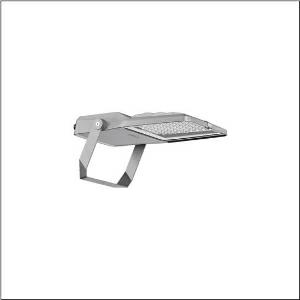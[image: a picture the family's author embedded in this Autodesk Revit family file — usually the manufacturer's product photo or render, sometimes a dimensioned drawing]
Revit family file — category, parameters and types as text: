
# Revit family: floodlight_fl_21_mini___pl64_5xa7776b4e1a_9990
name_source: partatom
category: Lighting Fixtures
units: mm (PartAtom-declared; Revit-internal decimal feet)

## family parameters
Cut with Voids When Loaded = No
Host = Face
Light Source = No
Part Type = Normal
Room Calculation Point = No
Round Connector Dimension = Use Diameter
Shared = No

## types (1)
- --- (1 x LED, 6260 lm, 45.7 W, 4000K)
    Apparent Load = 46 VA
    CIE Flux Codes = 28 80 98 100 100
    Color Rendering = 70
    Color Temperature = 4000K
    Default Elevation = 1800 mm
    Description = Floodlight FL 21 mini, floodlight, primary light control with lens, of PMMA, primary optical cover: protective disc, of toughened safety glass, transparent, light distribution: PL64, light emission: direct distribution, installation type: surface-mounted, LED, High Power LED, rated luminous flux: 6.260lm, luminous efficacy: 137lm/W, light colour: 740, colour temperature: 4000K, control gear: D4iSmart Interface (Zhaga), control: overheat protection, constant luminous flux control, time-dependent luminous flux control, flexible luminous flux parameterisation, pre-setting: logarithmic dimming characteristic, with terminal, 6-pole, mains connection: 220..240V, AC, 50/60Hz, start of lifetime: 46W, end of service life: 48W, reduction: 22W, mounting bracket, of diecast aluminium, powder-coated, Siteco® metallic grey (DB 702S), corrosivity category C5 mid according to DIN EN ISO 12944, suitable for swimming pools, chlorine-resistant, sealing non-destructively replaceable, mounting bracket, of steel, galvanised, powder-coated, Siteco® metallic grey (DB 702S), Smart Interface below and above, protection rating (complete): IP66, insulation class (complete): insulation class II (safety insulation), certification: CE, ENEC, VDE, protection symbol: D, impact resistance: IK08, permissible operating ambient temperature: -40..+40°C, permissible operating ambient temperature for outdoor applications: -40..+50°C, standard: DIN EN 12944, LABS conformity tested according to VDMA 24364:2018-05, packaging unit: 1 piece

Light Distribution: PL64
    Height = 70 mm
    Lamp = 1 x LED
    Lamp Light Flux = 6260 lm
    Lamp Power = 45.7 W
    Lamp count = 1
    Length = 485 mm
    Luminous efficacy = 137 lm/W
    Manufacturer = Siteco
    ModVariant = No
    Model = 5XA7776B4E1A
    Number of Poles = 1
    OnlyDefault = Yes
    Power Factor = 1
    Product Name = Floodlight FL 21 mini | PL64
    Product group = floodlight | pylon annexe
    ProductGroupID = 6200
    Protection Class = Protection class II
    Protection Degree = IP 66
    RLX_Detail_Level = 1
    RLX_Emergency_Light_Flux = 0 lm
    RLX_Emergency_Type = 0
    RLX_Emergency_Type_DB = No
    RlxData = <blob elided: 96001 chars, md5=5dcb8d71>
    Socket = socket
    Standby Power = 0 W
    System Light Flux = 6260 lm
    System Power = 46 W
    Type Comments = factory setting: luminous flux: 100 % | dim-lin: 254 | 463 mA
    Type Image = l_1006845.jpg
    URL = http://relux.com
    VarID = @adj_097154
    Voltage = 0 V
    Weight = 0.00 kg
    Width = 337 mm

## geometry (parser evidence)
native form markers: Blend x4, Sweep x12
no freeform markers — native parametric forms only
